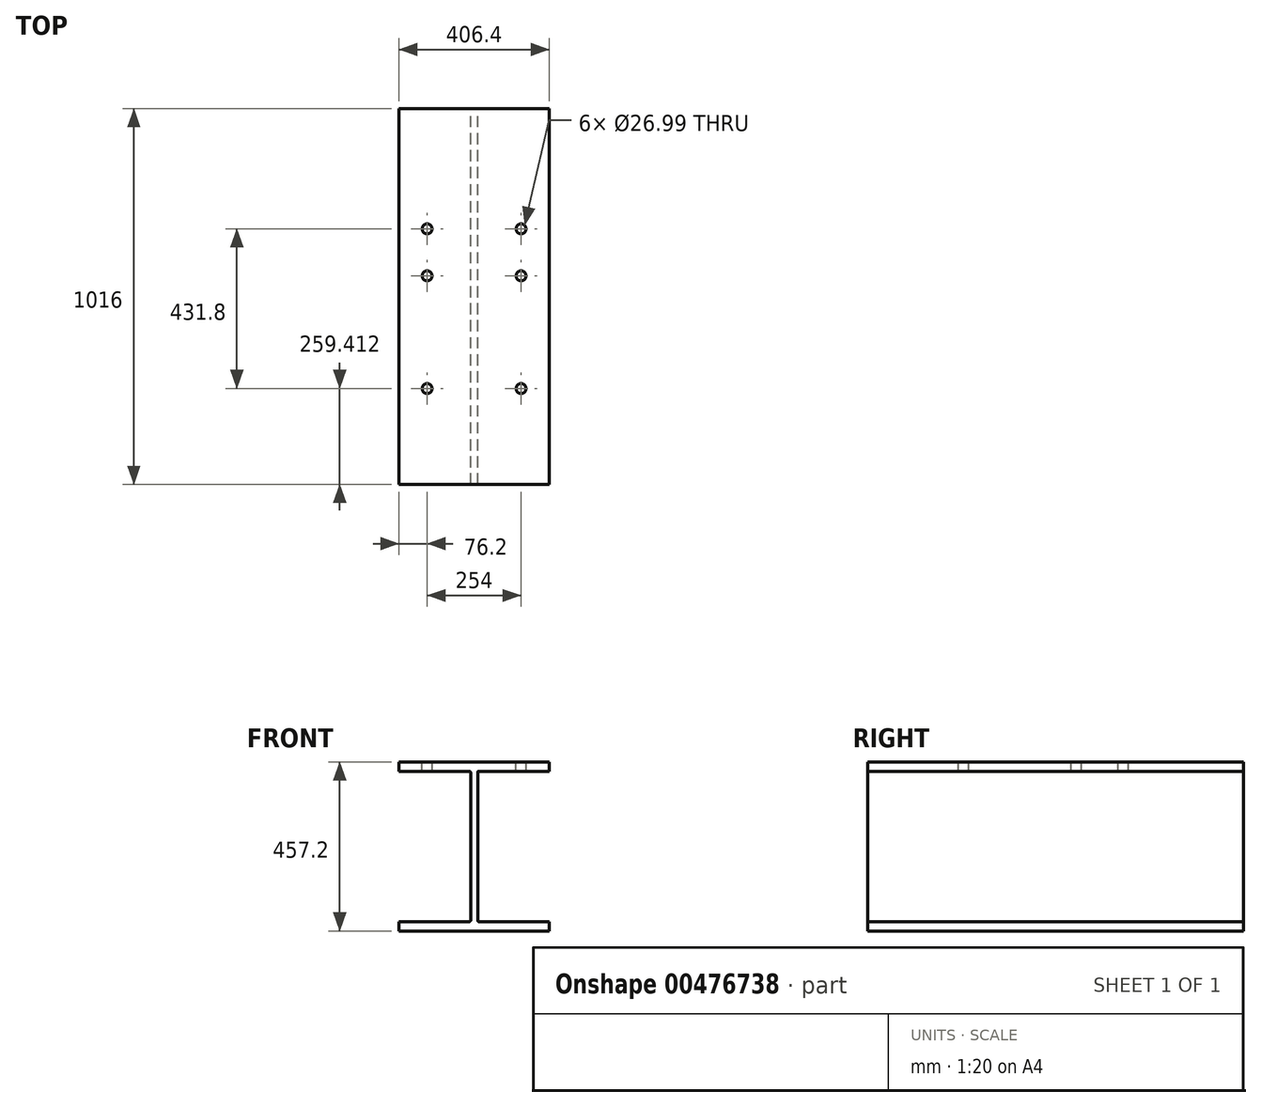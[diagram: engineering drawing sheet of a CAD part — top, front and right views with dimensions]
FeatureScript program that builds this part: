
annotation { "Feature Type Name" : "Feature", "Feature Type Description" : "" }
export const myFeature = defineFeature(function(context is Context, id is Id, definition is map)
    precondition{}
    {
        {
            var Q0;
            Q0=qCreatedBy(makeId("Front.planeOp"),FACE);
            var sketch = newSketch(context, id + "F0", { "sketchPlane" : qUnion([Q0])});
            skLineSegment(sketch, "E0", {"start": v(203.2, -203.2) * mm, "end": v(12.06, -203.2) * mm});
            skLineSegment(sketch, "E1", {"start": v(9.52, -200.66) * mm, "end": v(9.52, 200.66) * mm});
            skLineSegment(sketch, "E2", {"start": v(12.06, 203.2) * mm, "end": v(203.2, 203.2) * mm});
            skLineSegment(sketch, "E3", {"start": v(-203.2, 203.2) * mm, "end": v(-12.06, 203.2) * mm});
            skLineSegment(sketch, "E4", {"start": v(-9.53, 200.66) * mm, "end": v(-9.53, -200.66) * mm});
            skLineSegment(sketch, "E5", {"start": v(-12.06, -203.2) * mm, "end": v(-203.2, -203.2) * mm});
            skLineSegment(sketch, "E6", {"start": v(0, 0) * mm, "end": v(-9.52, 0) * mm, "construction": true});
            skLineSegment(sketch, "E7", {"start": v(0, 0) * mm, "end": v(9.52, 0) * mm, "construction": true});
            skLineSegment(sketch, "E8", {"start": v(0, 0) * mm, "end": v(0, 228.6) * mm, "construction": true});
            skLineSegment(sketch, "E9", {"start": v(0, 0) * mm, "end": v(0, -228.6) * mm, "construction": true});
            skPoint(sketch, "E10.visualSharp", {"position": v(-9.53, 203.2) * mm});
            skArc(sketch, "E10.filletArc", {"start": v(-9.52, 200.66) * mm, "mid": v(-10.27, 202.46) * mm, "end": v(-12.06, 203.2) * mm});
            skPoint(sketch, "E11.visualSharp", {"position": v(9.53, 203.2) * mm});
            skArc(sketch, "E11.filletArc", {"start": v(12.07, 203.2) * mm, "mid": v(10.27, 202.46) * mm, "end": v(9.52, 200.66) * mm});
            skPoint(sketch, "E12.visualSharp", {"position": v(9.53, -203.2) * mm});
            skArc(sketch, "E12.filletArc", {"start": v(9.52, -200.66) * mm, "mid": v(10.27, -202.46) * mm, "end": v(12.06, -203.2) * mm});
            skPoint(sketch, "E13.visualSharp", {"position": v(-9.53, -203.2) * mm});
            skArc(sketch, "E13.filletArc", {"start": v(-12.06, -203.2) * mm, "mid": v(-10.27, -202.46) * mm, "end": v(-9.52, -200.66) * mm});
            skPoint(sketch, "E14.visualSharp", {"position": v(-203.2, 228.6) * mm});
            skPoint(sketch, "E15.visualSharp", {"position": v(203.2, 228.6) * mm});
            skPoint(sketch, "E16.visualSharp", {"position": v(203.2, 203.2) * mm});
            skPoint(sketch, "E17.visualSharp", {"position": v(203.2, -228.6) * mm});
            skPoint(sketch, "E18.visualSharp", {"position": v(-203.2, -203.2) * mm});
            skPoint(sketch, "E19.visualSharp", {"position": v(-203.2, -228.6) * mm});
            skLineSegment(sketch, "E20", {"start": v(203.2, -203.2) * mm, "end": v(203.2, -228.6) * mm});
            skLineSegment(sketch, "E21", {"start": v(-203.2, -203.2) * mm, "end": v(-203.2, -228.6) * mm});
            skLineSegment(sketch, "E22", {"start": v(-203.2, 228.6) * mm, "end": v(-203.2, 203.2) * mm});
            skLineSegment(sketch, "E23", {"start": v(203.2, 228.6) * mm, "end": v(203.2, 203.2) * mm});
            skLineSegment(sketch, "E24", {"start": v(-203.2, 228.6) * mm, "end": v(203.2, 228.6) * mm});
            skLineSegment(sketch, "E25", {"start": v(-203.2, -228.6) * mm, "end": v(203.2, -228.6) * mm});
            skSolve(sketch);
        }
        {
            var Q0;
            Q0=makeQuery(id+"F0.imprint","IMPRINT",FACE,{"disambiguationData":[TD([[makeQuery(id+"F0.imprint","IMPRINT",EDGE,{"derivedFrom":sQuery(id+"F0.wireOp",EDGE,"E0")}),1.0]])]});
            extrude(context, id + "F1", {"entities" : qUnion([Q0]), "endBound" : BoundingType.SYMMETRIC, "depth" : 1016 * mm});
        }
        {
            var Q0;
            Q0=makeQuery(id+"F1.opExtrude","SWEPT_FACE",FACE,{"disambiguationData":[OSD([sQuery(id+"F0.wireOp",EDGE,"E24")])]});
            var sketch = newSketch(context, id + "F2", { "sketchPlane" : qUnion([Q0])});
            skPoint(sketch, "E26", {"position": v(-127, 183.21) * mm});
            skPoint(sketch, "E27", {"position": v(-127, 56.21) * mm});
            skPoint(sketch, "E28", {"position": v(-127, -248.59) * mm});
            skPoint(sketch, "E29", {"position": v(127, -248.59) * mm});
            skPoint(sketch, "E30", {"position": v(127, 56.21) * mm});
            skPoint(sketch, "E31", {"position": v(127, 183.21) * mm});
            skLineSegment(sketch, "E32", {"start": v(-127, 183.21) * mm, "end": v(-203.2, 183.21) * mm, "construction": true});
            skLineSegment(sketch, "E33", {"start": v(127, 183.21) * mm, "end": v(203.2, 183.21) * mm, "construction": true});
            skSolve(sketch);
        }
        {
            var Q0;
            Q0=sQuery(id+"F2.wireOp",VERTEX,"E26");
            var Q1;
            Q1=sQuery(id+"F2.wireOp",VERTEX,"E27");
            var Q2;
            Q2=sQuery(id+"F2.wireOp",VERTEX,"E28");
            var Q3;
            Q3=sQuery(id+"F2.wireOp",VERTEX,"E29");
            var Q4;
            Q4=sQuery(id+"F2.wireOp",VERTEX,"E30");
            var Q5;
            Q5=sQuery(id+"F2.wireOp",VERTEX,"E31");
            var Q6;
            Q6=makeQuery(id+"F1.opExtrude","SWEPT_BODY",BODY,{"disambiguationData":[OSD([sQuery(id+"F0.wireOp",EDGE,"E0"),sQuery(id+"F0.wireOp",EDGE,"E1"),sQuery(id+"F0.wireOp",EDGE,"E2"),sQuery(id+"F0.wireOp",EDGE,"E3"),sQuery(id+"F0.wireOp",EDGE,"E4"),sQuery(id+"F0.wireOp",EDGE,"E5"),sQuery(id+"F0.wireOp",EDGE,"E10.filletArc"),sQuery(id+"F0.wireOp",EDGE,"E11.filletArc"),sQuery(id+"F0.wireOp",EDGE,"E12.filletArc"),sQuery(id+"F0.wireOp",EDGE,"E13.filletArc"),sQuery(id+"F0.wireOp",EDGE,"E20"),sQuery(id+"F0.wireOp",EDGE,"E21"),sQuery(id+"F0.wireOp",EDGE,"E22"),sQuery(id+"F0.wireOp",EDGE,"E23"),sQuery(id+"F0.wireOp",EDGE,"E24"),sQuery(id+"F0.wireOp",EDGE,"E25")])]});
            hole(context, id + "F3", {"style" : HoleStyle.SIMPLE, "endStyle" : HoleEndStyle.BLIND, "holeDiameter" : 26.99 * mm, "holeDepth" : 25.4 * mm, "isTappedThrough" : true, "tappedDepth" : 12.7 * mm, "tapClearance" : 3, "locations" : qUnion([Q0, Q1, Q2, Q3, Q4, Q5]), "scope" : qUnion([Q6])});
        }
    });
